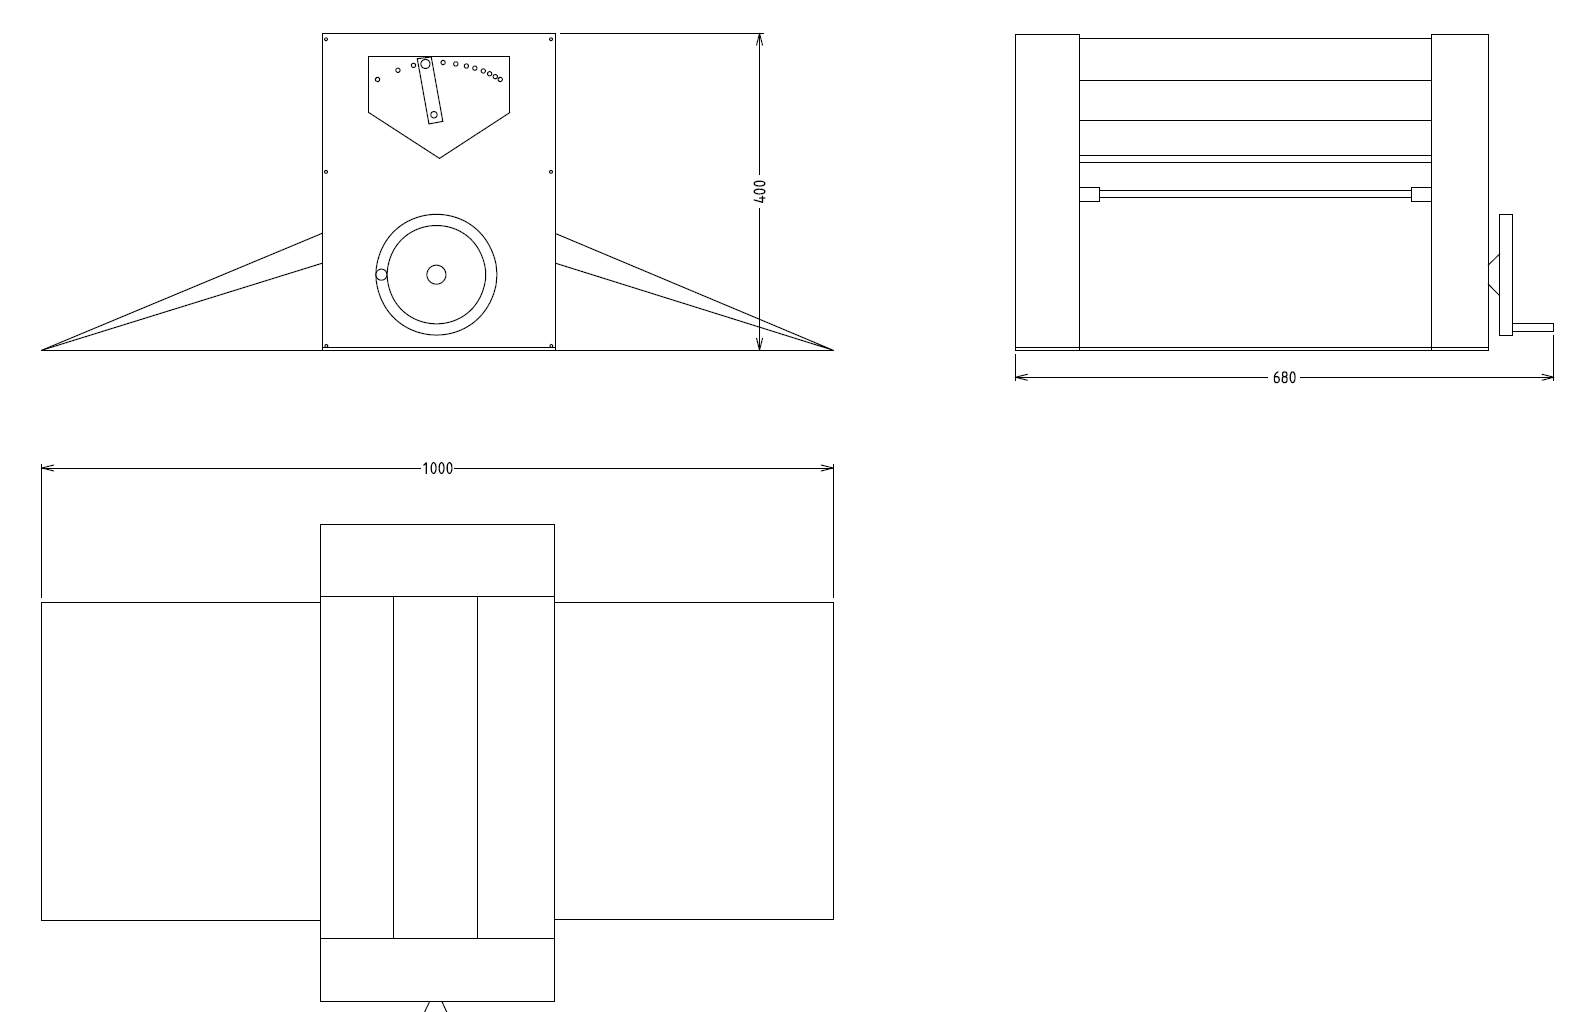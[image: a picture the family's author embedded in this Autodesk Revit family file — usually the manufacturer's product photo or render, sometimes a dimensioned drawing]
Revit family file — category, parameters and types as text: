
# Revit family: QF_DITOSAMA_601549_DLMP400
name_source: partatom
category: Specialty Equipment
revit_build: Autodesk Revit 2018 (Build: 20190510_1515(x64)
units: mm (PartAtom-declared; Revit-internal decimal feet)

## family parameters
Always vertical = Yes
Cut with Voids When Loaded = No
Part Type = Normal
Room Calculation Point = No
Round Connector Dimension = Use Diameter
Shared = No
Work Plane-Based = No

## types (1)
- QF_DITO SAMA_601549_DLMP400
    Accessory = Yes
    Cold Water Size = 0 mm
    Compressed Air Pressure = 0.0 Pa
    Compressed Air Size = 0 mm
    Compressed Air Volume = 0.0 L/s
    Condensate Return Size = 0 mm
    Cycle = 0 Hz
    Depth Actual = 680 mm  [stored 2.23097 ft]
    Description = HAND DOUGH SHEETER-REMOV.S/S FLAPS-400MM
    Direct Waste Size = 0 mm
    Gas Input Pressure = 0
    Gas KW = 0
    Gas Size = 0 mm
    HP = 0 HP
    Height Actual = 400 mm  [stored 1.31234 ft]
    Hot Water Size = 0 mm
    Item Number = 601549
    Length Actual = 1000 mm  [stored 3.28084 ft]
    Manufacturer = Dito Sama
    Model = DLMP400
    Phase = 0
    Refrigerant Compressor Remote = Yes
    Refrigeration Liquid Line Size = 0 mm
    Refrigeration Suction Line Size = 0 mm
    Steam Pounds per Hour = 0
    Steam Supply Maximum Pressure = 0.0 Pa
    Steam Supply Minimum Pressure = 0.0 Pa
    Steam Supply Size = 0 mm
    URL = http://www.ditosama.com
    URL Manufacturer = http://www.ditosama.com
    Volts = 0 V
    Watts = 0 W
    Weight = 35.00 kg

note: source unit labels omitted for Gas Input Pressure — the stored unit's dimension contradicts the parameter name (converter mislabeling)

note: [stored X ft] marks values corroborated as IEEE doubles in the binary element streams (Revit-internal decimal feet)

## geometry (parser evidence)
native form markers: Sweep x4
no freeform markers — native parametric forms only
